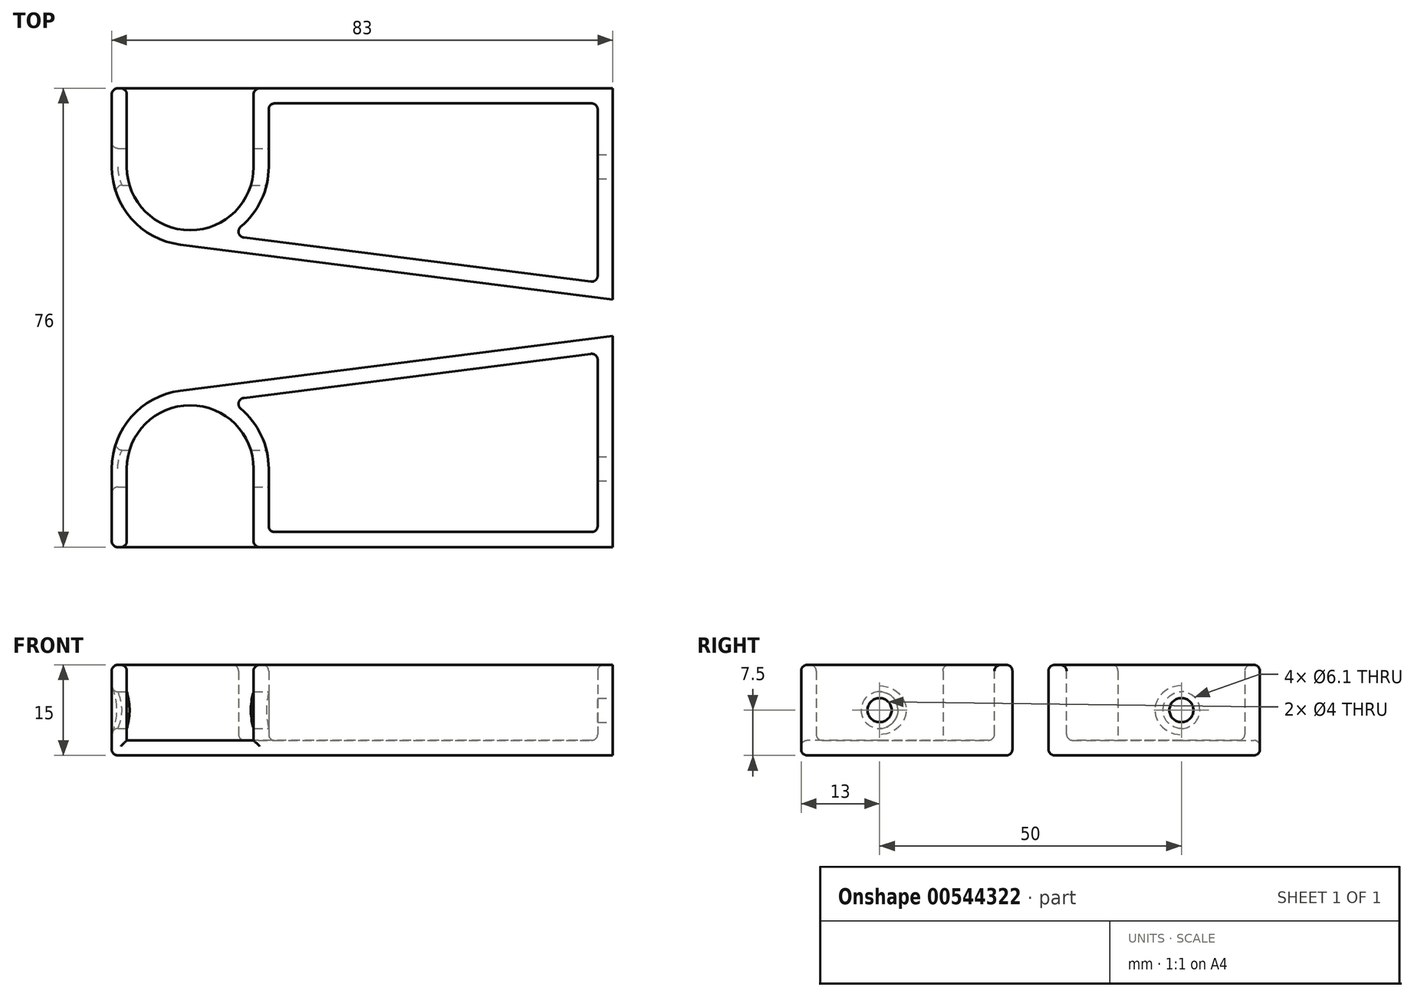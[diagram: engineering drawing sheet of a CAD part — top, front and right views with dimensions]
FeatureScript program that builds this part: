
annotation { "Feature Type Name" : "Feature", "Feature Type Description" : "" }
export const myFeature = defineFeature(function(context is Context, id is Id, definition is map)
    precondition{}
    {
        {
            var Q0;
            Q0=qCreatedBy(makeId("Top.planeOp"),FACE);
            var sketch = newSketch(context, id + "F0", { "sketchPlane" : qUnion([Q0])});
            skArc(sketch, "E0", {"start": v(-13, 0) * mm, "mid": v(-9.75, -8.6) * mm, "end": v(-1.64, -12.9) * mm});
            skArc(sketch, "E1", {"start": v(-10.5, 0) * mm, "mid": v(0, -10.5) * mm, "end": v(10.5, 0) * mm});
            skLineSegment(sketch, "E2", {"start": v(-13, 0) * mm, "end": v(-13, 13) * mm});
            skLineSegment(sketch, "E3", {"start": v(-13, 13) * mm, "end": v(70, 13) * mm});
            skLineSegment(sketch, "E4", {"start": v(70, 13) * mm, "end": v(70, -22) * mm});
            skLineSegment(sketch, "E5", {"start": v(-10.5, 0) * mm, "end": v(-10.5, 13) * mm});
            skLineSegment(sketch, "E6", {"start": v(10.5, 0) * mm, "end": v(10.5, 13) * mm});
            skLineSegment(sketch, "E7", {"start": v(70, -22) * mm, "end": v(-1.64, -12.9) * mm});
            skSolve(sketch);
        }
        {
            var Q0;
            Q0=makeQuery(id+"F0.imprint","IMPRINT",FACE,{"disambiguationData":[TD([[makeQuery(id+"F0.imprint","IMPRINT",EDGE,{"derivedFrom":sQuery(id+"F0.wireOp",EDGE,"E0")}),1.0]])]});
            extrude(context, id + "F1", {"entities" : qUnion([Q0]), "depth" : 15 * mm, "offsetDistance" : 25 * mm});
        }
        {
            var Q0;
            Q0=makeQuery(id+"F0.imprint","IMPRINT",FACE,{"disambiguationData":[TD([[makeQuery(id+"F0.imprint","IMPRINT",EDGE,{"derivedFrom":sQuery(id+"F0.wireOp",EDGE,"E1")}),1.0]])]});
            extrude(context, id + "F2", {"entities" : qUnion([Q0]), "operationType" : NewBodyOperationType.ADD, "depth" : 2.5 * mm, "offsetDistance" : 25 * mm});
        }
        {
            var Q0;
            Q0=makeQuery(id+"F1.opExtrude","CAP_FACE",FACE,{"disambiguationData":[OSD([sQuery(id+"F0.wireOp",EDGE,"E0"),sQuery(id+"F0.wireOp",EDGE,"E1"),sQuery(id+"F0.wireOp",EDGE,"E2"),sQuery(id+"F0.wireOp",EDGE,"E3"),sQuery(id+"F0.wireOp",EDGE,"E4"),sQuery(id+"F0.wireOp",EDGE,"E5"),sQuery(id+"F0.wireOp",EDGE,"E6"),sQuery(id+"F0.wireOp",EDGE,"E7")])],"isStart":false});
            shell(context, id + "F3", {"entities" : qUnion([Q0]), "thickness" : 2.5 * mm});
        }
        {
            var Q0;
            Q0=makeQuery(id+"F1.opExtrude","SWEPT_FACE",FACE,{"disambiguationData":[OSD([sQuery(id+"F0.wireOp",EDGE,"E4")])]});
            var sketch = newSketch(context, id + "F4", { "sketchPlane" : qUnion([Q0])});
            skCircle(sketch, "E8", {"center": v(0, 7.5) * mm, "radius": 2 * mm});
            skPoint(sketch, "E8.centerSnap0", {"position": v(13, 7.5) * mm});
            skSolve(sketch);
        }
        {
            var Q0;
            Q0 = qSketchRegion(id + "F4", true);
            var Q1;
            Q1=sQuery(id+"F4.wireOp",EDGE,"E8");
            extrude(context, id + "F5", {"entities" : qUnion([Q0]), "operationType" : NewBodyOperationType.REMOVE, "surfaceEntities" : qUnion([Q1]), "oppositeDirection" : true, "depth" : 25 * mm, "offsetDistance" : 25 * mm});
        }
        {
            var Q0;
            Q0=makeQuery(id+"F3.opShell","OFFSET_FACE",FACE,{"disambiguationData":[OSD([sQuery(id+"F0.wireOp",EDGE,"E4")])]});
            var sketch = newSketch(context, id + "F6", { "sketchPlane" : qUnion([Q0])});
            skCircle(sketch, "E9", {"center": v(0, 7.5) * mm, "radius": 3.05 * mm});
            skSolve(sketch);
        }
        {
            var Q0;
            Q0 = qSketchRegion(id + "F6", true);
            extrude(context, id + "F7", {"entities" : qUnion([Q0]), "operationType" : NewBodyOperationType.REMOVE, "endBound" : BoundingType.THROUGH_ALL, "depth" : 25 * mm, "offsetDistance" : 25 * mm});
        }
        {
            var Q0;
            {var subQ0=sQuery(id+"F0.wireOp",EDGE,"E7");Q0=makeQuery(id+"F3.opShell","OFFSET_EDGE",EDGE,{"disambiguationData":[OSD([subQ0]),TDD([makeQuery(id+"F1.opExtrude","CAP_EDGE",EDGE,{"disambiguationData":[OSD([subQ0])],"isStart":false})])]});}
            var Q1;
            Q1=makeQuery(id+"F3.opShell","OFFSET_EDGE",EDGE,{"disambiguationData":[OSD([sQuery(id+"F0.wireOp",EDGE,"E1")])]});
            var Q2;
            {var subQ0=sQuery(id+"F0.wireOp",EDGE,"E3");Q2=makeQuery(id+"F3.opShell","OFFSET_EDGE",EDGE,{"disambiguationData":[OSD([subQ0]),TDD([makeQuery(id+"F1.opExtrude","CAP_EDGE",EDGE,{"disambiguationData":[OSD([subQ0]),TDD([makeQuery(id+"F0.imprint","IMPRINT",EDGE,{"disambiguationData":[TD([[makeQuery(id+"F0.imprint","INTERSECT",VERTEX,{"derivedFrom":[subQ0,sQuery(id+"F0.wireOp",EDGE,"E4")]}),1.0]])],"derivedFrom":subQ0})])],"isStart":false})])]});}
            var Q3;
            {var subQ0=sQuery(id+"F0.wireOp",EDGE,"E4");Q3=makeQuery(id+"F3.opShell","OFFSET_EDGE",EDGE,{"disambiguationData":[OSD([subQ0]),TDD([makeQuery(id+"F1.opExtrude","CAP_EDGE",EDGE,{"disambiguationData":[OSD([subQ0])],"isStart":false})])]});}
            var Q4;
            Q4=makeQuery(id+"F1.opExtrude","CAP_EDGE",EDGE,{"disambiguationData":[OSD([sQuery(id+"F0.wireOp",EDGE,"E7")])],"isStart":false});
            var Q5;
            Q5=makeQuery(id+"F1.opExtrude","CAP_EDGE",EDGE,{"disambiguationData":[OSD([sQuery(id+"F0.wireOp",EDGE,"E6")])],"isStart":false});
            var Q6;
            {var subQ0=sQuery(id+"F0.wireOp",EDGE,"E3");Q6=makeQuery(id+"F1.opExtrude","CAP_EDGE",EDGE,{"disambiguationData":[OSD([subQ0]),TDD([makeQuery(id+"F0.imprint","IMPRINT",EDGE,{"disambiguationData":[TD([[makeQuery(id+"F0.imprint","INTERSECT",VERTEX,{"derivedFrom":[sQuery(id+"F0.wireOp",EDGE,"E2"),subQ0]}),-1.0]])],"derivedFrom":subQ0})])],"isStart":false});}
            var Q7;
            Q7=makeQuery(id+"F1.opExtrude","SWEPT_EDGE",EDGE,{"disambiguationData":[OSD([sQuery(id+"F0.wireOp",EDGE,"E3"),sQuery(id+"F0.wireOp",EDGE,"E5")])]});
            var Q8;
            {var subQ0=sQuery(id+"F0.wireOp",EDGE,"E3");Q8=makeQuery(id+"F1.opExtrude","CAP_EDGE",EDGE,{"disambiguationData":[OSD([subQ0]),TDD([makeQuery(id+"F0.imprint","IMPRINT",EDGE,{"disambiguationData":[TD([[makeQuery(id+"F0.imprint","INTERSECT",VERTEX,{"derivedFrom":[subQ0,sQuery(id+"F0.wireOp",EDGE,"E4")]}),1.0]])],"derivedFrom":subQ0})])],"isStart":false});}
            var Q9;
            Q9=makeQuery(id+"F1.opExtrude","SWEPT_EDGE",EDGE,{"disambiguationData":[OSD([sQuery(id+"F0.wireOp",EDGE,"E2"),sQuery(id+"F0.wireOp",EDGE,"E3")])]});
            var Q10;
            Q10=makeQuery(id+"F1.opExtrude","CAP_EDGE",EDGE,{"disambiguationData":[OSD([sQuery(id+"F0.wireOp",EDGE,"E2")])],"isStart":true});
            var Q11;
            Q11=makeQuery(id+"F2.opExtrude","CAP_EDGE",EDGE,{"disambiguationData":[OSD([sQuery(id+"F0.wireOp",EDGE,"E3")])],"isStart":false});
            var Q12;
            {var subQ0=sQuery(id+"F0.wireOp",EDGE,"E3");Q12=makeQuery(id+"F2.boolean.opBoolean","MERGE",EDGE,{"derivedFrom":[makeQuery(id+"F1.opExtrude","CAP_EDGE",EDGE,{"disambiguationData":[OSD([subQ0]),TDD([makeQuery(id+"F0.imprint","IMPRINT",EDGE,{"disambiguationData":[TD([[makeQuery(id+"F0.imprint","INTERSECT",VERTEX,{"derivedFrom":[sQuery(id+"F0.wireOp",EDGE,"E2"),subQ0]}),-1.0]])],"derivedFrom":subQ0})])],"isStart":true}),makeQuery(id+"F1.opExtrude","CAP_EDGE",EDGE,{"disambiguationData":[OSD([subQ0]),TDD([makeQuery(id+"F0.imprint","IMPRINT",EDGE,{"disambiguationData":[TD([[makeQuery(id+"F0.imprint","INTERSECT",VERTEX,{"derivedFrom":[subQ0,sQuery(id+"F0.wireOp",EDGE,"E4")]}),1.0]])],"derivedFrom":subQ0})])],"isStart":true}),makeQuery(id+"F2.opExtrude","CAP_EDGE",EDGE,{"disambiguationData":[OSD([subQ0])],"isStart":true})]});}
            var Q13;
            Q13=makeQuery(id+"F1.opExtrude","SWEPT_EDGE",EDGE,{"disambiguationData":[OSD([sQuery(id+"F0.wireOp",EDGE,"E3"),sQuery(id+"F0.wireOp",EDGE,"E6")])]});
            var Q14;
            Q14=makeQuery(id+"F7.boolean.opBoolean","INTERSECT",EDGE,{"derivedFrom":[makeQuery(id+"F1.opExtrude","SWEPT_FACE",FACE,{"disambiguationData":[OSD([sQuery(id+"F0.wireOp",EDGE,"E2")])]}),makeQuery(id+"F7.opExtrude","SWEPT_FACE",FACE,{"disambiguationData":[OSD([sQuery(id+"F6.wireOp",EDGE,"E9")])]})]});
            var Q15;
            Q15=makeQuery(id+"F3.opShell","OFFSET_EDGE",EDGE,{"disambiguationData":[OSD([sQuery(id+"F0.wireOp",EDGE,"E3"),sQuery(id+"F0.wireOp",EDGE,"E6")])]});
            var Q16;
            Q16=makeQuery(id+"F3.opShell","TWEAK_EDGE",EDGE,{"derivedFrom":[makeQuery(id+"F1.opExtrude","SWEPT_FACE",FACE,{"disambiguationData":[OSD([sQuery(id+"F0.wireOp",EDGE,"E7")])]}),makeQuery(id+"F1.opExtrude","SWEPT_FACE",FACE,{"disambiguationData":[OSD([sQuery(id+"F0.wireOp",EDGE,"E1")])]})]});
            var Q17;
            {var subQ0=sQuery(id+"F0.wireOp",EDGE,"E7");Q17=makeQuery(id+"F3.opShell","OFFSET_EDGE",EDGE,{"disambiguationData":[OSD([subQ0]),TDD([makeQuery(id+"F1.opExtrude","CAP_EDGE",EDGE,{"disambiguationData":[OSD([subQ0])],"isStart":true})])]});}
            var Q18;
            {var subQ0=sQuery(id+"F0.wireOp",EDGE,"E1");var subQ1=sQuery(id+"F0.wireOp",EDGE,"E6");var subQ2=sQuery(id+"F0.wireOp",EDGE,"E5");var subQ3=sQuery(id+"F0.wireOp",EDGE,"E3");Q18=makeQuery(id+"F3.opShell","TWEAK_EDGE",EDGE,{"derivedFrom":[makeQuery(id+"F2.boolean.opBoolean","MERGE",FACE,{"derivedFrom":[makeQuery(id+"F1.opExtrude","CAP_FACE",FACE,{"disambiguationData":[OSD([sQuery(id+"F0.wireOp",EDGE,"E0"),subQ0,sQuery(id+"F0.wireOp",EDGE,"E2"),subQ3,sQuery(id+"F0.wireOp",EDGE,"E4"),subQ2,subQ1,sQuery(id+"F0.wireOp",EDGE,"E7")])],"isStart":true}),makeQuery(id+"F2.opExtrude","CAP_FACE",FACE,{"disambiguationData":[OSD([subQ0,subQ3,subQ2,subQ1])],"isStart":true})]}),makeQuery(id+"F1.opExtrude","SWEPT_FACE",FACE,{"disambiguationData":[OSD([subQ0])]})]});}
            var Q19;
            {var subQ0=sQuery(id+"F0.wireOp",EDGE,"E3");Q19=makeQuery(id+"F3.opShell","OFFSET_EDGE",EDGE,{"disambiguationData":[OSD([subQ0]),TDD([makeQuery(id+"F2.boolean.opBoolean","MERGE",EDGE,{"derivedFrom":[makeQuery(id+"F1.opExtrude","CAP_EDGE",EDGE,{"disambiguationData":[OSD([subQ0]),TDD([makeQuery(id+"F0.imprint","IMPRINT",EDGE,{"disambiguationData":[TD([[makeQuery(id+"F0.imprint","INTERSECT",VERTEX,{"derivedFrom":[sQuery(id+"F0.wireOp",EDGE,"E2"),subQ0]}),-1.0]])],"derivedFrom":subQ0})])],"isStart":true}),makeQuery(id+"F1.opExtrude","CAP_EDGE",EDGE,{"disambiguationData":[OSD([subQ0]),TDD([makeQuery(id+"F0.imprint","IMPRINT",EDGE,{"disambiguationData":[TD([[makeQuery(id+"F0.imprint","INTERSECT",VERTEX,{"derivedFrom":[subQ0,sQuery(id+"F0.wireOp",EDGE,"E4")]}),1.0]])],"derivedFrom":subQ0})])],"isStart":true}),makeQuery(id+"F2.opExtrude","CAP_EDGE",EDGE,{"disambiguationData":[OSD([subQ0])],"isStart":true})]})])]});}
            var Q20;
            {var subQ0=sQuery(id+"F0.wireOp",EDGE,"E4");Q20=makeQuery(id+"F3.opShell","OFFSET_EDGE",EDGE,{"disambiguationData":[OSD([subQ0]),TDD([makeQuery(id+"F1.opExtrude","CAP_EDGE",EDGE,{"disambiguationData":[OSD([subQ0])],"isStart":true})])]});}
            var Q21;
            Q21=makeQuery(id+"F3.opShell","OFFSET_EDGE",EDGE,{"disambiguationData":[OSD([sQuery(id+"F0.wireOp",EDGE,"E3"),sQuery(id+"F0.wireOp",EDGE,"E4")])]});
            var Q22;
            Q22=makeQuery(id+"F3.opShell","OFFSET_EDGE",EDGE,{"disambiguationData":[OSD([sQuery(id+"F0.wireOp",EDGE,"E4"),sQuery(id+"F0.wireOp",EDGE,"E7")])]});
            var Q23;
            Q23=makeQuery(id+"F2.opExtrude","CAP_EDGE",EDGE,{"disambiguationData":[OSD([sQuery(id+"F0.wireOp",EDGE,"E5")])],"isStart":false});
            fillet(context, id + "F8", {"entities" : qUnion([Q0, Q1, Q2, Q3, Q4, Q5, Q6, Q7, Q8, Q9, Q10, Q11, Q12, Q13, Q14, Q15, Q16, Q17, Q18, Q19, Q20, Q21, Q22, Q23]), "radius" : 1 * mm, "tangentPropagation" : true, "allowEdgeOverflow" : false});
        }
        {
            var Q0;
            Q0=makeQuery(id+"F1.opExtrude","SWEPT_BODY",BODY,{"disambiguationData":[OSD([sQuery(id+"F0.wireOp",EDGE,"E0"),sQuery(id+"F0.wireOp",EDGE,"E1"),sQuery(id+"F0.wireOp",EDGE,"E2"),sQuery(id+"F0.wireOp",EDGE,"E3"),sQuery(id+"F0.wireOp",EDGE,"E4"),sQuery(id+"F0.wireOp",EDGE,"E5"),sQuery(id+"F0.wireOp",EDGE,"E6"),sQuery(id+"F0.wireOp",EDGE,"E7")])]});
            transform(context, id + "F9", {"entities" : qUnion([Q0]), "transformType" : TransformType.TRANSLATION_3D, "dx" : 0 * mm, "dy" : 25 * mm, "dz" : 0 * mm, "makeCopy" : false});
        }
        {
            var Q0;
            Q0=makeQuery(id+"F1.opExtrude","SWEPT_BODY",BODY,{"disambiguationData":[OSD([sQuery(id+"F0.wireOp",EDGE,"E0"),sQuery(id+"F0.wireOp",EDGE,"E1"),sQuery(id+"F0.wireOp",EDGE,"E2"),sQuery(id+"F0.wireOp",EDGE,"E3"),sQuery(id+"F0.wireOp",EDGE,"E4"),sQuery(id+"F0.wireOp",EDGE,"E5"),sQuery(id+"F0.wireOp",EDGE,"E6"),sQuery(id+"F0.wireOp",EDGE,"E7")])]});
            var Q1;
            Q1=qCreatedBy(makeId("Front.planeOp"),FACE);
            mirror(context, id + "F10", {"entities" : qUnion([Q0]), "mirrorPlane" : qUnion([Q1])});
        }
    });
